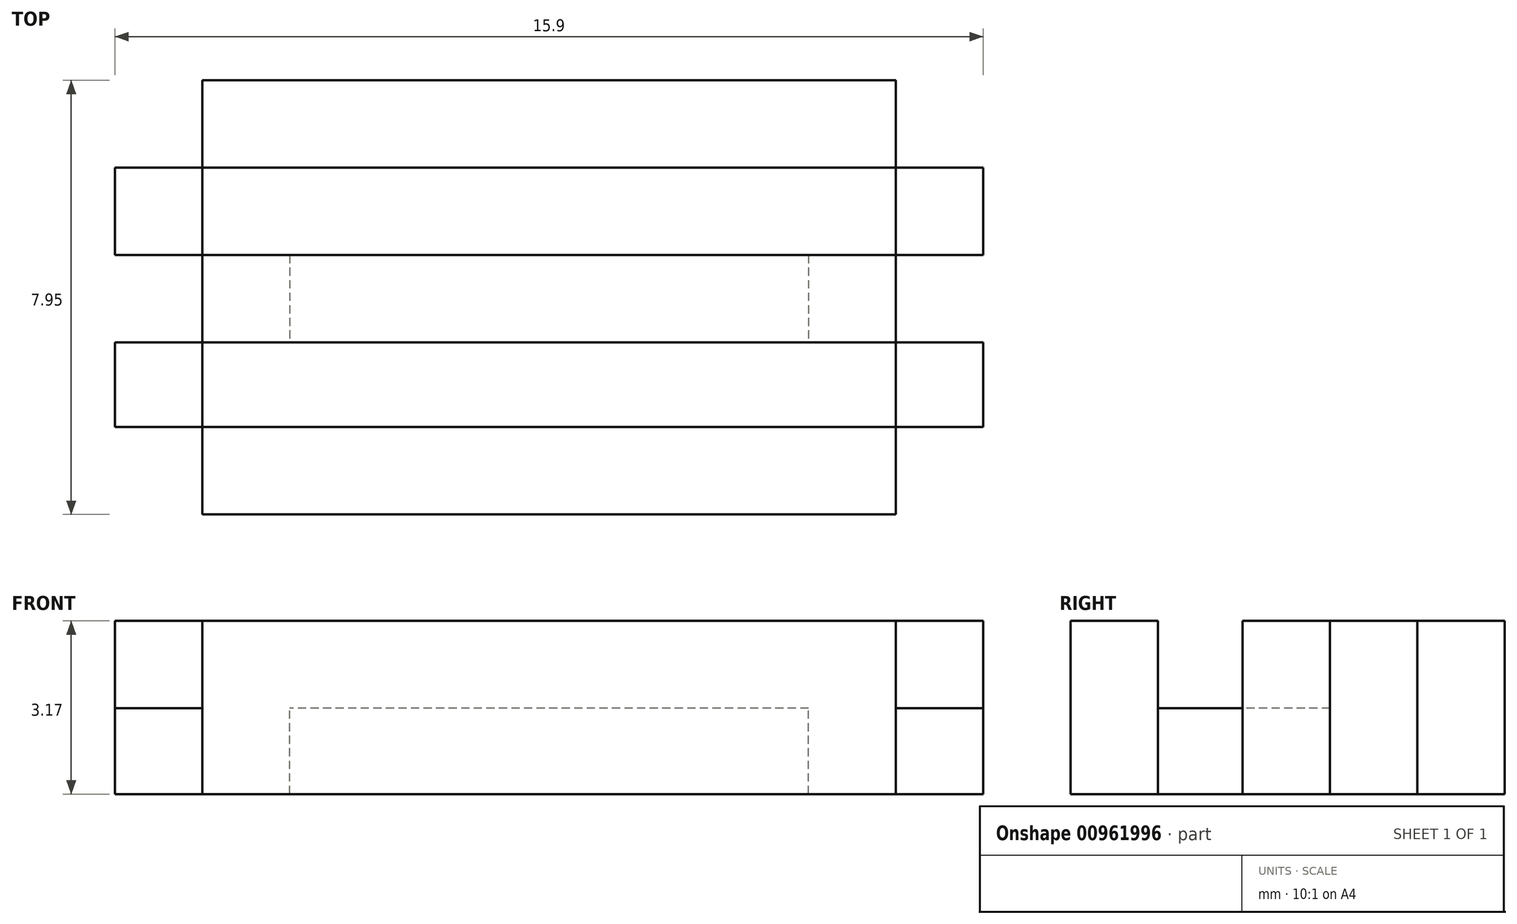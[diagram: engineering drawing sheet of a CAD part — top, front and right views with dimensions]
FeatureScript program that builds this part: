
annotation { "Feature Type Name" : "Feature", "Feature Type Description" : "" }
export const myFeature = defineFeature(function(context is Context, id is Id, definition is map)
    precondition{}
    {
        {
            var Q0;
            Q0=qCreatedBy(makeId("Top.planeOp"),FACE);
            var sketch = newSketch(context, id + "F0", { "sketchPlane" : qUnion([Q0])});
            skLineSegment(sketch, "E0.bottom", {"start": v(-13.03, 31.01) * mm, "end": v(2.87, 31.01) * mm});
            skLineSegment(sketch, "E0.top", {"start": v(-13.03, 23.06) * mm, "end": v(2.87, 23.06) * mm});
            skLineSegment(sketch, "E0.left", {"start": v(-13.03, 31.01) * mm, "end": v(-13.03, 23.06) * mm});
            skLineSegment(sketch, "E0.right", {"start": v(2.87, 31.01) * mm, "end": v(2.87, 23.06) * mm});
            skLineSegment(sketch, "E1.top", {"start": v(-13.03, 29.41) * mm, "end": v(2.87, 29.41) * mm});
            skLineSegment(sketch, "E1.left", {"start": v(-13.03, 31.01) * mm, "end": v(-13.03, 29.41) * mm});
            skLineSegment(sketch, "E1.right", {"start": v(2.87, 31.01) * mm, "end": v(2.87, 29.41) * mm});
            skLineSegment(sketch, "E2.bottom", {"start": v(-13.03, 27.81) * mm, "end": v(2.87, 27.81) * mm});
            skLineSegment(sketch, "E2.top", {"start": v(-13.03, 26.21) * mm, "end": v(2.87, 26.21) * mm});
            skLineSegment(sketch, "E2.left", {"start": v(-13.03, 27.81) * mm, "end": v(-13.03, 26.21) * mm});
            skLineSegment(sketch, "E2.right", {"start": v(2.87, 27.81) * mm, "end": v(2.87, 26.21) * mm});
            skLineSegment(sketch, "E3.bottom", {"start": v(-13.03, 24.66) * mm, "end": v(2.87, 24.66) * mm});
            skLineSegment(sketch, "E3.left", {"start": v(-13.03, 24.66) * mm, "end": v(-13.03, 23.06) * mm});
            skLineSegment(sketch, "E3.right", {"start": v(2.87, 24.66) * mm, "end": v(2.87, 23.06) * mm});
            skLineSegment(sketch, "E4", {"start": v(-11.43, 31.01) * mm, "end": v(-11.43, 23.06) * mm});
            skLineSegment(sketch, "E5", {"start": v(1.27, 31.01) * mm, "end": v(1.27, 23.06) * mm});
            skSolve(sketch);
        }
        {
            var Q0;
            {var subQ0=sQuery(id+"F0.wireOp",EDGE,"E4");var subQ1=sQuery(id+"F0.wireOp",EDGE,"E0.bottom");var subQ2=makeQuery(id+"F0.imprint","INTERSECT",VERTEX,{"derivedFrom":[subQ1,subQ0]});Q0=makeQuery(id+"F0.imprint","IMPRINT",FACE,{"disambiguationData":[TD([[makeQuery(id+"F0.imprint","IMPRINT",EDGE,{"disambiguationData":[TD([[subQ2,-1.0]])],"derivedFrom":subQ1}),-1.0]])]});}
            var Q1;
            {var subQ0=sQuery(id+"F0.wireOp",EDGE,"E4");var subQ1=sQuery(id+"F0.wireOp",EDGE,"E1.top");var subQ2=makeQuery(id+"F0.imprint","INTERSECT",VERTEX,{"derivedFrom":[subQ1,subQ0]});Q1=makeQuery(id+"F0.imprint","IMPRINT",FACE,{"disambiguationData":[TD([[makeQuery(id+"F0.imprint","IMPRINT",EDGE,{"disambiguationData":[TD([[subQ2,-1.0]])],"derivedFrom":subQ1}),-1.0]])]});}
            var Q2;
            {var subQ0=sQuery(id+"F0.wireOp",EDGE,"E4");var subQ1=sQuery(id+"F0.wireOp",EDGE,"E2.top");var subQ2=makeQuery(id+"F0.imprint","INTERSECT",VERTEX,{"derivedFrom":[subQ1,subQ0]});Q2=makeQuery(id+"F0.imprint","IMPRINT",FACE,{"disambiguationData":[TD([[makeQuery(id+"F0.imprint","IMPRINT",EDGE,{"disambiguationData":[TD([[subQ2,-1.0]])],"derivedFrom":subQ1}),-1.0]])]});}
            var Q3;
            {var subQ0=sQuery(id+"F0.wireOp",EDGE,"E4");var subQ1=sQuery(id+"F0.wireOp",EDGE,"E3.bottom");var subQ2=makeQuery(id+"F0.imprint","INTERSECT",VERTEX,{"derivedFrom":[subQ1,subQ0]});Q3=makeQuery(id+"F0.imprint","IMPRINT",FACE,{"disambiguationData":[TD([[makeQuery(id+"F0.imprint","IMPRINT",EDGE,{"disambiguationData":[TD([[subQ2,-1.0]])],"derivedFrom":subQ1}),-1.0]])]});}
            var Q4;
            {var subQ0=sQuery(id+"F0.wireOp",EDGE,"E4");var subQ1=sQuery(id+"F0.wireOp",EDGE,"E2.bottom");var subQ2=makeQuery(id+"F0.imprint","INTERSECT",VERTEX,{"derivedFrom":[subQ1,subQ0]});Q4=makeQuery(id+"F0.imprint","IMPRINT",FACE,{"disambiguationData":[TD([[makeQuery(id+"F0.imprint","IMPRINT",EDGE,{"disambiguationData":[TD([[subQ2,-1.0]])],"derivedFrom":subQ1}),-1.0]])]});}
            var Q5;
            {var subQ0=sQuery(id+"F0.wireOp",EDGE,"E1.left");Q5=makeQuery(id+"F0.imprint","IMPRINT",FACE,{"disambiguationData":[TD([[makeQuery(id+"F0.imprint","IMPRINT",EDGE,{"derivedFrom":subQ0}),1.0]])]});}
            var Q6;
            {var subQ0=sQuery(id+"F0.wireOp",EDGE,"E2.left");Q6=makeQuery(id+"F0.imprint","IMPRINT",FACE,{"disambiguationData":[TD([[makeQuery(id+"F0.imprint","IMPRINT",EDGE,{"derivedFrom":subQ0}),1.0]])]});}
            var Q7;
            {var subQ0=sQuery(id+"F0.wireOp",EDGE,"E3.left");Q7=makeQuery(id+"F0.imprint","IMPRINT",FACE,{"disambiguationData":[TD([[makeQuery(id+"F0.imprint","IMPRINT",EDGE,{"derivedFrom":subQ0}),1.0]])]});}
            var Q8;
            {var subQ0=sQuery(id+"F0.wireOp",EDGE,"E1.right");Q8=makeQuery(id+"F0.imprint","IMPRINT",FACE,{"disambiguationData":[TD([[makeQuery(id+"F0.imprint","IMPRINT",EDGE,{"derivedFrom":subQ0}),-1.0]])]});}
            var Q9;
            {var subQ0=sQuery(id+"F0.wireOp",EDGE,"E2.right");Q9=makeQuery(id+"F0.imprint","IMPRINT",FACE,{"disambiguationData":[TD([[makeQuery(id+"F0.imprint","IMPRINT",EDGE,{"derivedFrom":subQ0}),-1.0]])]});}
            var Q10;
            {var subQ0=sQuery(id+"F0.wireOp",EDGE,"E3.right");Q10=makeQuery(id+"F0.imprint","IMPRINT",FACE,{"disambiguationData":[TD([[makeQuery(id+"F0.imprint","IMPRINT",EDGE,{"derivedFrom":subQ0}),-1.0]])]});}
            var Q11;
            {var subQ0=sQuery(id+"F0.wireOp",EDGE,"E1.top");var subQ5=sQuery(id+"F0.wireOp",EDGE,"E4");var subQ6=makeQuery(id+"F0.imprint","INTERSECT",VERTEX,{"derivedFrom":[subQ0,subQ5]});Q11=makeQuery(id+"F0.imprint","IMPRINT",FACE,{"disambiguationData":[TD([[makeQuery(id+"F0.imprint","IMPRINT",EDGE,{"disambiguationData":[TD([[subQ6,-1.0]])],"derivedFrom":subQ5}),-1.0]])]});}
            var Q12;
            {var subQ3=sQuery(id+"F0.wireOp",EDGE,"E2.top");var subQ5=sQuery(id+"F0.wireOp",EDGE,"E4");var subQ6=makeQuery(id+"F0.imprint","INTERSECT",VERTEX,{"derivedFrom":[subQ3,subQ5]});Q12=makeQuery(id+"F0.imprint","IMPRINT",FACE,{"disambiguationData":[TD([[makeQuery(id+"F0.imprint","IMPRINT",EDGE,{"disambiguationData":[TD([[subQ6,-1.0]])],"derivedFrom":subQ5}),-1.0]])]});}
            var Q13;
            {var subQ0=sQuery(id+"F0.wireOp",EDGE,"E1.top");var subQ5=sQuery(id+"F0.wireOp",EDGE,"E5");var subQ6=makeQuery(id+"F0.imprint","INTERSECT",VERTEX,{"derivedFrom":[subQ0,subQ5]});Q13=makeQuery(id+"F0.imprint","IMPRINT",FACE,{"disambiguationData":[TD([[makeQuery(id+"F0.imprint","IMPRINT",EDGE,{"disambiguationData":[TD([[subQ6,-1.0]])],"derivedFrom":subQ5}),1.0]])]});}
            var Q14;
            {var subQ3=sQuery(id+"F0.wireOp",EDGE,"E2.top");var subQ5=sQuery(id+"F0.wireOp",EDGE,"E5");var subQ6=makeQuery(id+"F0.imprint","INTERSECT",VERTEX,{"derivedFrom":[subQ3,subQ5]});Q14=makeQuery(id+"F0.imprint","IMPRINT",FACE,{"disambiguationData":[TD([[makeQuery(id+"F0.imprint","IMPRINT",EDGE,{"disambiguationData":[TD([[subQ6,-1.0]])],"derivedFrom":subQ5}),1.0]])]});}
            extrude(context, id + "F1", {"entities" : qUnion([Q0, Q1, Q2, Q3, Q4, Q5, Q6, Q7, Q8, Q9, Q10, Q11, Q12, Q13, Q14]), "depth" : 3.17 * mm, "offsetDistance" : 25.4 * mm});
        }
        {
            var Q0;
            Q0=makeQuery(id+"F1.opExtrude","CAP_FACE",FACE,{"disambiguationData":[OSD([sQuery(id+"F0.wireOp",EDGE,"E0.left"),sQuery(id+"F0.wireOp",EDGE,"E0.right"),sQuery(id+"F0.wireOp",EDGE,"E0.bottom"),sQuery(id+"F0.wireOp",EDGE,"E1.left"),sQuery(id+"F0.wireOp",EDGE,"E1.right"),sQuery(id+"F0.wireOp",EDGE,"E2.left"),sQuery(id+"F0.wireOp",EDGE,"E2.right"),sQuery(id+"F0.wireOp",EDGE,"E0.top"),sQuery(id+"F0.wireOp",EDGE,"E3.left"),sQuery(id+"F0.wireOp",EDGE,"E3.right")])],"isStart":true});
            shell(context, id + "F2", {"entities" : qUnion([Q0]), "thickness" : 1.6 * mm});
        }
        {
            var Q0;
            {var subQ0=sQuery(id+"F0.wireOp",EDGE,"E4");var subQ1=sQuery(id+"F0.wireOp",EDGE,"E2.top");var subQ2=makeQuery(id+"F0.imprint","INTERSECT",VERTEX,{"derivedFrom":[subQ1,subQ0]});Q0=makeQuery(id+"F0.imprint","IMPRINT",FACE,{"disambiguationData":[TD([[makeQuery(id+"F0.imprint","IMPRINT",EDGE,{"disambiguationData":[TD([[subQ2,-1.0]])],"derivedFrom":subQ1}),-1.0]])]});}
            var Q1;
            {var subQ0=sQuery(id+"F0.wireOp",EDGE,"E4");var subQ1=sQuery(id+"F0.wireOp",EDGE,"E1.top");var subQ2=makeQuery(id+"F0.imprint","INTERSECT",VERTEX,{"derivedFrom":[subQ1,subQ0]});Q1=makeQuery(id+"F0.imprint","IMPRINT",FACE,{"disambiguationData":[TD([[makeQuery(id+"F0.imprint","IMPRINT",EDGE,{"disambiguationData":[TD([[subQ2,-1.0]])],"derivedFrom":subQ1}),-1.0]])]});}
            extrude(context, id + "F3", {"entities" : qUnion([Q0, Q1]), "operationType" : NewBodyOperationType.REMOVE, "depth" : 25.4 * mm, "offsetDistance" : 25.4 * mm});
        }
        {
            var Q0;
            Q0=makeQuery(id+"F1.opExtrude","CAP_FACE",FACE,{"disambiguationData":[OSD([sQuery(id+"F0.wireOp",EDGE,"E0.left"),sQuery(id+"F0.wireOp",EDGE,"E0.right"),sQuery(id+"F0.wireOp",EDGE,"E0.bottom"),sQuery(id+"F0.wireOp",EDGE,"E1.left"),sQuery(id+"F0.wireOp",EDGE,"E1.right"),sQuery(id+"F0.wireOp",EDGE,"E2.left"),sQuery(id+"F0.wireOp",EDGE,"E2.right"),sQuery(id+"F0.wireOp",EDGE,"E0.top"),sQuery(id+"F0.wireOp",EDGE,"E3.left"),sQuery(id+"F0.wireOp",EDGE,"E3.right")])],"isStart":false});
            var sketch = newSketch(context, id + "F4", { "sketchPlane" : qUnion([Q0])});
            skLineSegment(sketch, "E6.0.0", {"start": v(1.27, 29.41) * mm, "end": v(-11.43, 29.41) * mm});
            skLineSegment(sketch, "E6.0.1", {"start": v(-11.43, 29.41) * mm, "end": v(-11.43, 27.81) * mm});
            skLineSegment(sketch, "E6.0.2", {"start": v(-11.43, 27.81) * mm, "end": v(1.27, 27.81) * mm});
            skLineSegment(sketch, "E6.0.3", {"start": v(1.27, 27.81) * mm, "end": v(1.27, 29.41) * mm});
            skLineSegment(sketch, "E7.0.0", {"start": v(1.27, 26.21) * mm, "end": v(-11.43, 26.21) * mm});
            skLineSegment(sketch, "E7.0.1", {"start": v(-11.43, 26.21) * mm, "end": v(-11.43, 24.66) * mm});
            skLineSegment(sketch, "E7.0.2", {"start": v(-11.43, 24.66) * mm, "end": v(1.27, 24.66) * mm});
            skLineSegment(sketch, "E7.0.3", {"start": v(1.27, 24.66) * mm, "end": v(1.27, 26.21) * mm});
            skLineSegment(sketch, "E8.0", {"start": v(1.27, 31.01) * mm, "end": v(1.27, 23.06) * mm});
            skLineSegment(sketch, "E9.0", {"start": v(2.87, 31.01) * mm, "end": v(2.87, 23.06) * mm});
            skLineSegment(sketch, "E10.0", {"start": v(-13.03, 31.01) * mm, "end": v(-13.03, 23.06) * mm});
            skPoint(sketch, "E11.0", {"position": v(-11.43, 27.04) * mm});
            skLineSegment(sketch, "E12.0", {"start": v(-11.43, 31.01) * mm, "end": v(-11.43, 23.06) * mm});
            skLineSegment(sketch, "E13.0", {"start": v(-13.03, 27.81) * mm, "end": v(2.87, 27.81) * mm});
            skLineSegment(sketch, "E14.0", {"start": v(-13.03, 29.41) * mm, "end": v(2.87, 29.41) * mm});
            skLineSegment(sketch, "E15.0", {"start": v(-13.03, 26.21) * mm, "end": v(2.87, 26.21) * mm});
            skLineSegment(sketch, "E16.0", {"start": v(-13.03, 24.66) * mm, "end": v(2.87, 24.66) * mm});
            skLineSegment(sketch, "E17", {"start": v(-13.03, 29.41) * mm, "end": v(-11.43, 29.41) * mm});
            skLineSegment(sketch, "E18", {"start": v(-13.03, 29.41) * mm, "end": v(-13.03, 27.81) * mm});
            skLineSegment(sketch, "E19", {"start": v(-13.03, 27.81) * mm, "end": v(-11.43, 27.81) * mm});
            skLineSegment(sketch, "E20", {"start": v(-11.43, 29.41) * mm, "end": v(1.27, 29.41) * mm});
            skLineSegment(sketch, "E21", {"start": v(1.27, 29.41) * mm, "end": v(1.27, 27.81) * mm});
            skLineSegment(sketch, "E22", {"start": v(1.27, 27.81) * mm, "end": v(-11.43, 27.81) * mm});
            skLineSegment(sketch, "E23", {"start": v(-11.43, 27.81) * mm, "end": v(-11.43, 29.41) * mm});
            skLineSegment(sketch, "E24", {"start": v(1.27, 29.41) * mm, "end": v(2.87, 29.41) * mm});
            skLineSegment(sketch, "E25", {"start": v(2.87, 29.41) * mm, "end": v(2.87, 27.81) * mm});
            skLineSegment(sketch, "E26", {"start": v(2.87, 27.81) * mm, "end": v(1.27, 27.81) * mm});
            skLineSegment(sketch, "E27", {"start": v(-11.43, 26.21) * mm, "end": v(-13.03, 26.21) * mm});
            skLineSegment(sketch, "E28", {"start": v(-13.03, 26.21) * mm, "end": v(-13.03, 24.66) * mm});
            skLineSegment(sketch, "E29", {"start": v(-13.03, 24.66) * mm, "end": v(-11.43, 24.66) * mm});
            skLineSegment(sketch, "E30", {"start": v(-11.43, 24.66) * mm, "end": v(-11.43, 26.21) * mm});
            skLineSegment(sketch, "E31", {"start": v(-11.43, 26.21) * mm, "end": v(1.27, 26.21) * mm});
            skLineSegment(sketch, "E32", {"start": v(2.87, 26.21) * mm, "end": v(2.87, 24.66) * mm});
            skSolve(sketch);
        }
        {
            var Q0;
            Q0=makeQuery(id+"F4.imprint","IMPRINT",FACE,{"disambiguationData":[TD([[makeQuery(id+"F4.imprint","IMPRINT",EDGE,{"derivedFrom":sQuery(id+"F4.wireOp",EDGE,"E21")}),-1.0]])]});
            var Q1;
            {var subQ2=sQuery(id+"F4.wireOp",EDGE,"E15.0");Q1=makeQuery(id+"F4.imprint","IMPRINT",FACE,{"disambiguationData":[TD([[makeQuery(id+"F4.imprint","IMPRINT",EDGE,{"derivedFrom":subQ2}),-1.0]])]});}
            var Q2;
            Q2=makeQuery(id+"F4.imprint","IMPRINT",FACE,{"disambiguationData":[TD([[makeQuery(id+"F4.imprint","IMPRINT",EDGE,{"derivedFrom":sQuery(id+"F4.wireOp",EDGE,"E17")}),-1.0]])]});
            var Q3;
            Q3=makeQuery(id+"F4.imprint","IMPRINT",FACE,{"disambiguationData":[TD([[makeQuery(id+"F4.imprint","IMPRINT",EDGE,{"derivedFrom":sQuery(id+"F4.wireOp",EDGE,"E27")}),1.0]])]});
            extrude(context, id + "F5", {"entities" : qUnion([Q0, Q1, Q2, Q3]), "operationType" : NewBodyOperationType.REMOVE, "oppositeDirection" : true, "depth" : 1.6 * mm, "offsetDistance" : 25.4 * mm});
        }
    });
